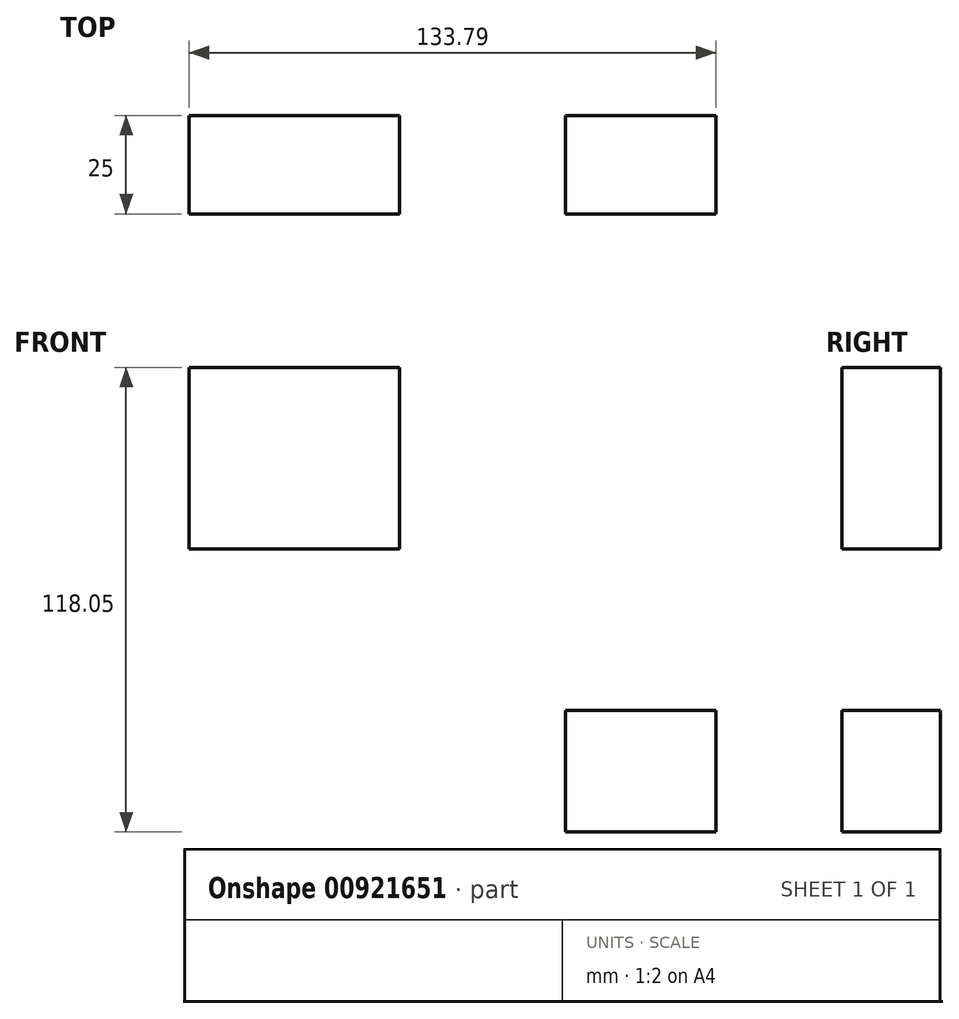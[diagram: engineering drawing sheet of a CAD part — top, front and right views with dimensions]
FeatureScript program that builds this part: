
annotation { "Feature Type Name" : "Feature", "Feature Type Description" : "" }
export const myFeature = defineFeature(function(context is Context, id is Id, definition is map)
    precondition{}
    {
        {
            var Q0;
            Q0=qCreatedBy(makeId("Front.planeOp"),FACE);
            var sketch = newSketch(context, id + "F0", { "sketchPlane" : qUnion([Q0])});
            skLineSegment(sketch, "E0.bottom", {"start": v(-128.6, -8.85) * mm, "end": v(-75.19, -8.85) * mm});
            skLineSegment(sketch, "E0.top", {"start": v(-128.6, 37.24) * mm, "end": v(-75.19, 37.24) * mm});
            skLineSegment(sketch, "E0.left", {"start": v(-128.6, -8.85) * mm, "end": v(-128.6, 37.24) * mm});
            skLineSegment(sketch, "E0.right", {"start": v(-75.19, -8.85) * mm, "end": v(-75.19, 37.24) * mm});
            skPoint(sketch, "E0.middle", {"position": v(-101.89, 14.2) * mm});
            skLineSegment(sketch, "E1.bottom", {"start": v(-33.03, -80.8) * mm, "end": v(5.2, -80.8) * mm});
            skLineSegment(sketch, "E1.top", {"start": v(-33.03, -49.9) * mm, "end": v(5.2, -49.9) * mm});
            skLineSegment(sketch, "E1.left", {"start": v(-33.03, -80.8) * mm, "end": v(-33.03, -49.9) * mm});
            skLineSegment(sketch, "E1.right", {"start": v(5.2, -80.8) * mm, "end": v(5.2, -49.9) * mm});
            skPoint(sketch, "E1.middle", {"position": v(-13.91, -65.35) * mm});
            skSolve(sketch);
        }
        {
            var Q0;
            Q0=makeQuery(id+"F0.imprint","IMPRINT",FACE,{"disambiguationData":[TD([[makeQuery(id+"F0.imprint","IMPRINT",EDGE,{"derivedFrom":sQuery(id+"F0.wireOp",EDGE,"E0.bottom")}),1.0]])]});
            var Q1;
            Q1=makeQuery(id+"F0.imprint","IMPRINT",FACE,{"disambiguationData":[TD([[makeQuery(id+"F0.imprint","IMPRINT",EDGE,{"derivedFrom":sQuery(id+"F0.wireOp",EDGE,"E1.bottom")}),1.0]])]});
            extrude(context, id + "F1", {"entities" : qUnion([Q0, Q1]), "depth" : 25 * mm, "offsetDistance" : 25 * mm});
        }
    });
